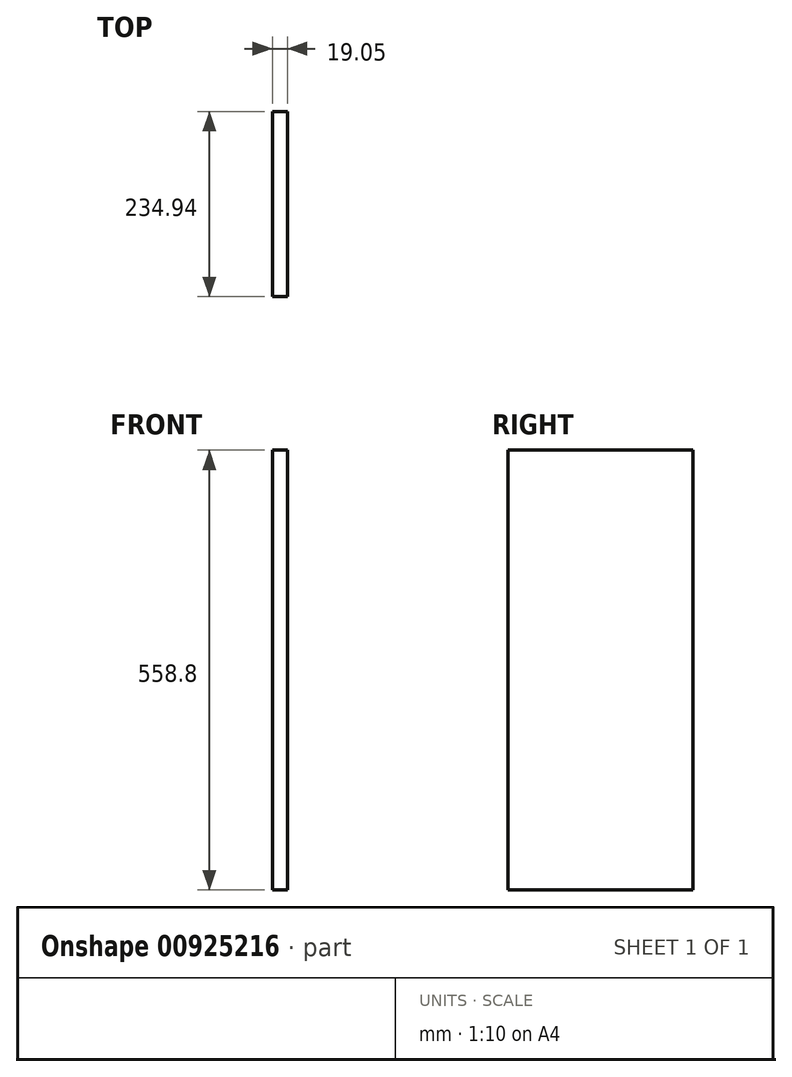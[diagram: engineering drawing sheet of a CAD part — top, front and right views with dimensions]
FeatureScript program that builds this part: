
annotation { "Feature Type Name" : "Feature", "Feature Type Description" : "" }
export const myFeature = defineFeature(function(context is Context, id is Id, definition is map)
    precondition{}
    {
        {
            var Q0;
            Q0=qCreatedBy(makeId("Right.planeOp"),FACE);
            var sketch = newSketch(context, id + "F0", { "sketchPlane" : qUnion([Q0])});
            skLineSegment(sketch, "E0.bottom", {"start": v(117.47, 279.4) * mm, "end": v(-117.48, 279.4) * mm});
            skLineSegment(sketch, "E0.top", {"start": v(117.48, -279.4) * mm, "end": v(-117.47, -279.4) * mm});
            skLineSegment(sketch, "E0.left", {"start": v(117.47, 279.4) * mm, "end": v(117.48, -279.4) * mm});
            skLineSegment(sketch, "E0.right", {"start": v(-117.48, 279.4) * mm, "end": v(-117.47, -279.4) * mm});
            skPoint(sketch, "E0.middle", {"position": v(0, 0) * mm});
            skSolve(sketch);
        }
        {
            var Q0;
            Q0 = qSketchRegion(id + "F0", true);
            extrude(context, id + "F1", {"entities" : qUnion([Q0]), "depth" : 19.05 * mm, "offsetDistance" : 25.4 * mm});
        }
    });
